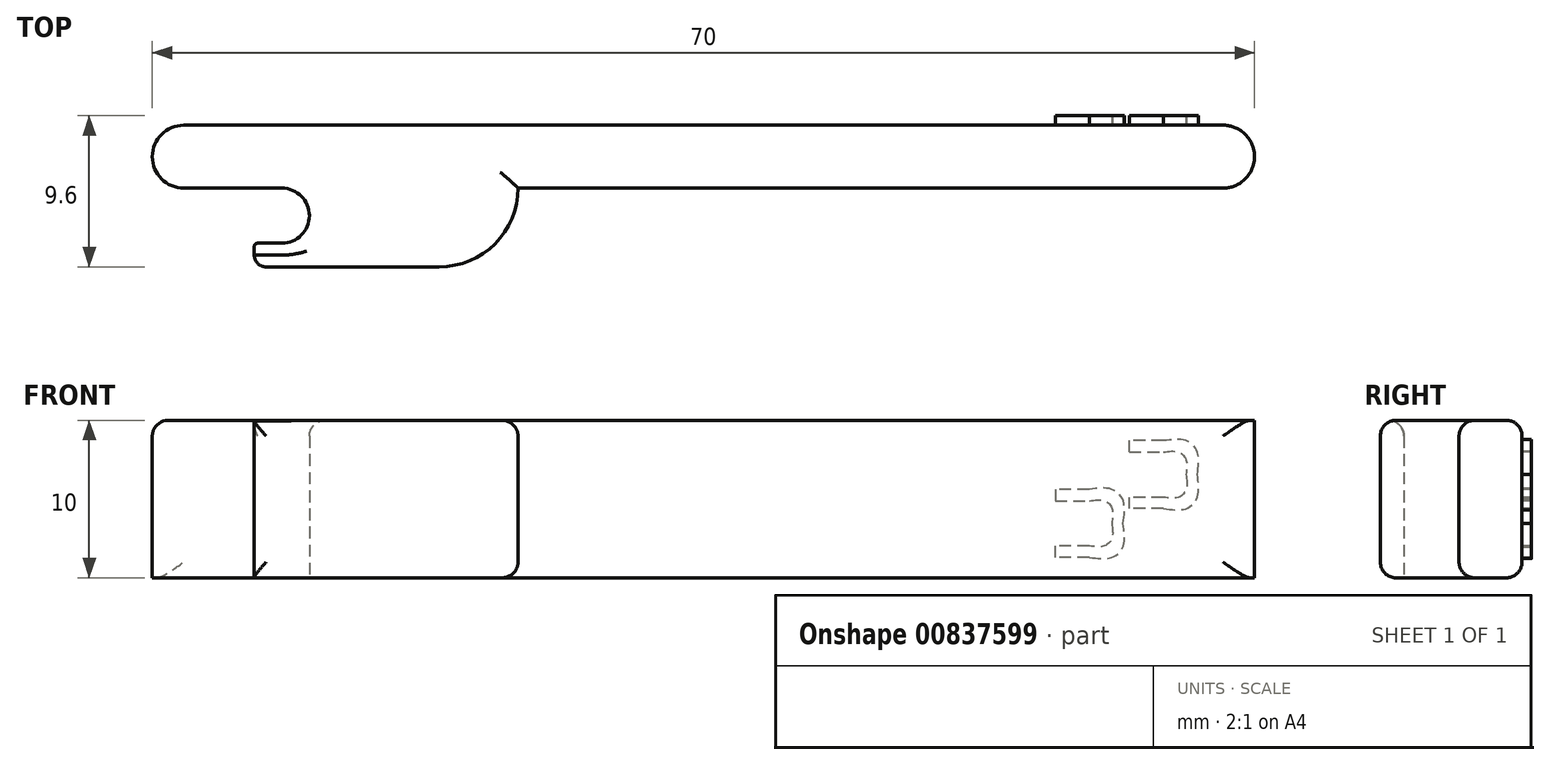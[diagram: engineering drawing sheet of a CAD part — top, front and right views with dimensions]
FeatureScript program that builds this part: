
annotation { "Feature Type Name" : "Feature", "Feature Type Description" : "" }
export const myFeature = defineFeature(function(context is Context, id is Id, definition is map)
    precondition{}
    {
        {
            var Q0;
            Q0=qCreatedBy(makeId("Top.planeOp"),FACE);
            var sketch = newSketch(context, id + "F0", { "sketchPlane" : qUnion([Q0])});
            skLineSegment(sketch, "E0.bottom", {"start": v(-26.18, 4) * mm, "end": v(39.82, 4) * mm});
            skLineSegment(sketch, "E0.top", {"start": v(-26.18, 0) * mm, "end": v(-19.95, 0) * mm});
            skLineSegment(sketch, "E0.left", {"start": v(-28.18, 2) * mm, "end": v(-28.18, 2) * mm});
            skLineSegment(sketch, "E0.right", {"start": v(41.82, 2) * mm, "end": v(41.82, 2) * mm});
            skLineSegment(sketch, "E1.bottom", {"start": v(-4.95, 0) * mm, "end": v(-4.36, 0) * mm});
            skLineSegment(sketch, "E2", {"start": v(-18.18, -6.06) * mm, "end": v(-18.18, 4) * mm, "construction": true});
            skPoint(sketch, "E3.visualSharp", {"position": v(-28.18, 0) * mm});
            skArc(sketch, "E3.filletArc", {"start": v(-28.18, 2) * mm, "mid": v(-27.6, 0.59) * mm, "end": v(-26.18, 0) * mm});
            skPoint(sketch, "E4.visualSharp", {"position": v(-28.18, 4) * mm});
            skArc(sketch, "E4.filletArc", {"start": v(-26.18, 4) * mm, "mid": v(-27.6, 3.41) * mm, "end": v(-28.18, 2) * mm});
            skArc(sketch, "E5", {"start": v(-19.95, -3.5) * mm, "mid": v(-18.2, -1.75) * mm, "end": v(-19.95, 0) * mm});
            skLineSegment(sketch, "E6.top", {"start": v(-19.95, -5) * mm, "end": v(-9.95, -5) * mm});
            skLineSegment(sketch, "E6.right", {"start": v(-4.95, 0) * mm, "end": v(-4.95, 0) * mm});
            skLineSegment(sketch, "E7.bottom", {"start": v(-19.95, -3.5) * mm, "end": v(-21.5, -3.5) * mm});
            skLineSegment(sketch, "E7.top", {"start": v(-19.95, -5) * mm, "end": v(-20.95, -5) * mm});
            skLineSegment(sketch, "E7.right", {"start": v(-21.7, -3.7) * mm, "end": v(-21.7, -4.25) * mm});
            skPoint(sketch, "E8.visualSharp", {"position": v(-21.7, -5) * mm});
            skArc(sketch, "E8.filletArc", {"start": v(-21.7, -4.25) * mm, "mid": v(-21.48, -4.78) * mm, "end": v(-20.95, -5) * mm});
            skPoint(sketch, "E9.visualSharp", {"position": v(-21.7, -3.5) * mm});
            skArc(sketch, "E9.filletArc", {"start": v(-21.5, -3.5) * mm, "mid": v(-21.64, -3.56) * mm, "end": v(-21.7, -3.7) * mm});
            skPoint(sketch, "E10.visualSharp", {"position": v(-4.95, -5) * mm});
            skArc(sketch, "E10.filletArc", {"start": v(-9.95, -5) * mm, "mid": v(-6.41, -3.54) * mm, "end": v(-4.95, 0) * mm});
            skPoint(sketch, "E11.visualSharp", {"position": v(41.82, 4) * mm});
            skArc(sketch, "E11.filletArc", {"start": v(41.82, 2) * mm, "mid": v(41.24, 3.41) * mm, "end": v(39.82, 4) * mm});
            skPoint(sketch, "E12.visualSharp", {"position": v(41.82, 0) * mm});
            skArc(sketch, "E12.filletArc", {"start": v(39.82, 0) * mm, "mid": v(41.24, 0.59) * mm, "end": v(41.82, 2) * mm});
            skLineSegment(sketch, "E13.trimOffspring", {"start": v(-4.95, 0) * mm, "end": v(39.82, 0) * mm});
            skSolve(sketch);
        }
        {
            var Q0;
            Q0=makeQuery(id+"F0.imprint","IMPRINT",FACE,{"disambiguationData":[TD([[makeQuery(id+"F0.imprint","IMPRINT",EDGE,{"derivedFrom":sQuery(id+"F0.wireOp",EDGE,"E0.bottom")}),-1.0]])]});
            extrude(context, id + "F1", {"entities" : qUnion([Q0]), "depth" : 10 * mm, "offsetDistance" : 25 * mm});
        }
        {
            var Q0;
            Q0=makeQuery(id+"F1.opExtrude","CAP_EDGE",EDGE,{"disambiguationData":[OSD([sQuery(id+"F0.wireOp",EDGE,"E13.trimOffspring")])],"isStart":false});
            var Q1;
            Q1=makeQuery(id+"F1.opExtrude","CAP_EDGE",EDGE,{"disambiguationData":[OSD([sQuery(id+"F0.wireOp",EDGE,"E10.filletArc")])],"isStart":false});
            var Q2;
            Q2=makeQuery(id+"F1.opExtrude","CAP_EDGE",EDGE,{"disambiguationData":[OSD([sQuery(id+"F0.wireOp",EDGE,"E10.filletArc")])],"isStart":true});
            var Q3;
            Q3=makeQuery(id+"F1.opExtrude","CAP_EDGE",EDGE,{"disambiguationData":[OSD([sQuery(id+"F0.wireOp",EDGE,"E6.top"),sQuery(id+"F0.wireOp",EDGE,"E7.top")])],"isStart":true});
            var Q4;
            Q4=makeQuery(id+"F1.opExtrude","CAP_EDGE",EDGE,{"disambiguationData":[OSD([sQuery(id+"F0.wireOp",EDGE,"E13.trimOffspring")])],"isStart":true});
            var Q5;
            Q5=makeQuery(id+"F1.opExtrude","CAP_EDGE",EDGE,{"disambiguationData":[OSD([sQuery(id+"F0.wireOp",EDGE,"E0.bottom")])],"isStart":true});
            var Q6;
            Q6=makeQuery(id+"F1.opExtrude","CAP_EDGE",EDGE,{"disambiguationData":[OSD([sQuery(id+"F0.wireOp",EDGE,"E0.bottom")])],"isStart":false});
            fillet(context, id + "F2", {"entities" : qUnion([Q0, Q1, Q2, Q3, Q4, Q5, Q6]), "radius" : 1 * mm, "allowEdgeOverflow" : false});
        }
        {
            var Q0;
            Q0=makeQuery(id+"F1.opExtrude","SWEPT_FACE",FACE,{"disambiguationData":[OSD([sQuery(id+"F0.wireOp",EDGE,"E0.bottom")])]});
            var sketch = newSketch(context, id + "F3", { "sketchPlane" : qUnion([Q0])});
            skLineSegment(sketch, "E14", {"start": v(-31.33, 2.02) * mm, "end": v(-29.17, 2.02) * mm});
            skLineSegment(sketch, "E15", {"start": v(-31.33, 5.62) * mm, "end": v(-29.17, 5.62) * mm});
            skLineSegment(sketch, "E16", {"start": v(-29.17, 5.62) * mm, "end": v(-29.17, 4.9) * mm});
            skLineSegment(sketch, "E17", {"start": v(-29.17, 4.9) * mm, "end": v(-31.33, 4.9) * mm});
            skFitSpline(sketch, "E18", {"points": [v(-31.33, 1.3) * mm, v(-32.77, 1.3) * mm, v(-33.49, 2.02) * mm, v(-33.49, 3.46) * mm]});
            skFitSpline(sketch, "E19", {"points": [v(-33.49, 3.46) * mm, v(-33.49, 4.9) * mm, v(-32.77, 5.62) * mm, v(-31.33, 5.62) * mm]});
            skFitSpline(sketch, "E20", {"points": [v(-31.33, 4.9) * mm, v(-32.29, 4.9) * mm, v(-32.77, 4.42) * mm, v(-32.77, 3.46) * mm]});
            skFitSpline(sketch, "E21", {"points": [v(-32.77, 3.46) * mm, v(-32.77, 2.5) * mm, v(-32.29, 2.02) * mm, v(-31.33, 2.02) * mm]});
            skLineSegment(sketch, "E22", {"start": v(-31.33, 1.3) * mm, "end": v(-29.17, 1.3) * mm});
            skLineSegment(sketch, "E23", {"start": v(-29.17, 1.3) * mm, "end": v(-29.17, 2.02) * mm});
            skLineSegment(sketch, "E24", {"start": v(-36.22, 5.11) * mm, "end": v(-33.88, 5.11) * mm});
            skLineSegment(sketch, "E25", {"start": v(-36.04, 8.7) * mm, "end": v(-33.88, 8.7) * mm});
            skLineSegment(sketch, "E26", {"start": v(-33.88, 7.99) * mm, "end": v(-36.04, 7.99) * mm});
            skFitSpline(sketch, "E27", {"points": [v(-36.04, 4.4) * mm, v(-37.47, 4.4) * mm, v(-38.2, 5.11) * mm, v(-38.2, 6.55) * mm]});
            skFitSpline(sketch, "E28", {"points": [v(-38.2, 6.55) * mm, v(-38.2, 7.99) * mm, v(-37.47, 8.7) * mm, v(-36.04, 8.7) * mm]});
            skFitSpline(sketch, "E29", {"points": [v(-36.04, 7.99) * mm, v(-37, 7.99) * mm, v(-37.47, 7.5) * mm, v(-37.47, 6.55) * mm]});
            skFitSpline(sketch, "E30", {"points": [v(-37.47, 6.55) * mm, v(-37.47, 5.6) * mm, v(-37, 5.11) * mm, v(-36.04, 5.11) * mm]});
            skLineSegment(sketch, "E31", {"start": v(-36.04, 4.4) * mm, "end": v(-33.88, 4.4) * mm});
            skLineSegment(sketch, "E32", {"start": v(-33.88, 4.4) * mm, "end": v(-33.88, 5.11) * mm});
            skLineSegment(sketch, "E33", {"start": v(-33.88, 7.99) * mm, "end": v(-33.88, 8.7) * mm});
            skSolve(sketch);
        }
        {
            var Q0;
            Q0=makeQuery(id+"F3.imprint","IMPRINT",FACE,{"disambiguationData":[TD([[makeQuery(id+"F3.imprint","IMPRINT",EDGE,{"derivedFrom":sQuery(id+"F3.wireOp",EDGE,"E14")}),-1.0]])]});
            var Q1;
            Q1=makeQuery(id+"F3.imprint","IMPRINT",FACE,{"disambiguationData":[TD([[makeQuery(id+"F3.imprint","IMPRINT",EDGE,{"derivedFrom":sQuery(id+"F3.wireOp",EDGE,"E25")}),-1.0]])]});
            extrude(context, id + "F4", {"entities" : qUnion([Q0, Q1]), "operationType" : NewBodyOperationType.ADD, "depth" : 0.6 * mm, "offsetDistance" : 25 * mm});
        }
    });
